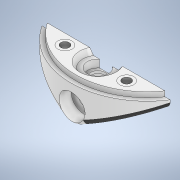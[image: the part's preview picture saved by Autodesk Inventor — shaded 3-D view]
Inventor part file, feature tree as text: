
AUTODESK INVENTOR PART (.ipt)
format: ipt  version: 2020 (Build 240168000, 168)  size: 330,752 bytes
history: native  units: in
note: dims shown in document units (in); Inventor stores cm internally (conversion verified against a paired STEP export)
features: sketch x6, extrude x3, hole x3, revolve x2, plane x2, fillet x2
ambient origin geometry x8: Origin, YZ Plane, XZ Plane, XY Plane, X Axis, Y Axis, Z Axis, Center Point
bodies: Solid1 (feature_tree)
feature tree (18):
  sketch  "Sketch1"  dims[d2=1.745in d3=0.126in]
  revolve  "Revolution1"  [1 undecoded]
  extrude  "Extrusion1"  Depth=0.25in
  extrude  "Extrusion3"  Depth=1.0in
  plane  "Work Plane3"
  hole  "Hole3"  [1 undecoded]
  plane  "Work Plane6"
  hole  "Hole5"  [1 undecoded]
  revolve  "Revolution2"  [1 undecoded]
  extrude  "Extrusion13"  Depth=0.5in
  fillet  "Fillet3"  Radius=0.375in
  fillet  "Fillet1"  Radius=0.375in
  hole  "Hole6"  [1 undecoded]
  sketch  "Sketch2"  dims[d5=0.25in d7=0.25in]
  sketch  "Sketch9"  dims[d9=180.0deg d10=1.0in]
  sketch  "Sketch19"  dims[d11=1.85in d12=0.0in d16=1.382in d17=0.0in]
  sketch  "Sketch21"  dims[d46=1.25in d47=1.5in]
  sketch  "Sketch23"  dims[d48=0.205in d49=0.75in d50=0.3438in d51=1.0in d52=0.5635in d53=1.0in d54=0.8108in d76=0.0312in d85=0.5in d86=0.266in d87=0.75in d88=0.625in d89=0.313in d90=0.5635in d91=1.0in d92=0.8108in d93=0.375in d95=0.375in d99=1.2in d102=90.0deg d103=0.2in d104=0.0in d110=0.125in d111=0.5in d112=0.2184in d113=0.4359in d114=0.5625in d115=0.25in d116=0.51in d119=0.35in d120=0.75in d121=0.51in d122=0.188in d123=0.5635in d124=0.25in d125=0.0in d126=1.85in d117=0.5635in d118=0.75in]
note: 5 required parameter values undecoded (feature->parameter linkage not recoverable at this tier; creation-order binding heuristic only, values carry confidence <= 0.55)